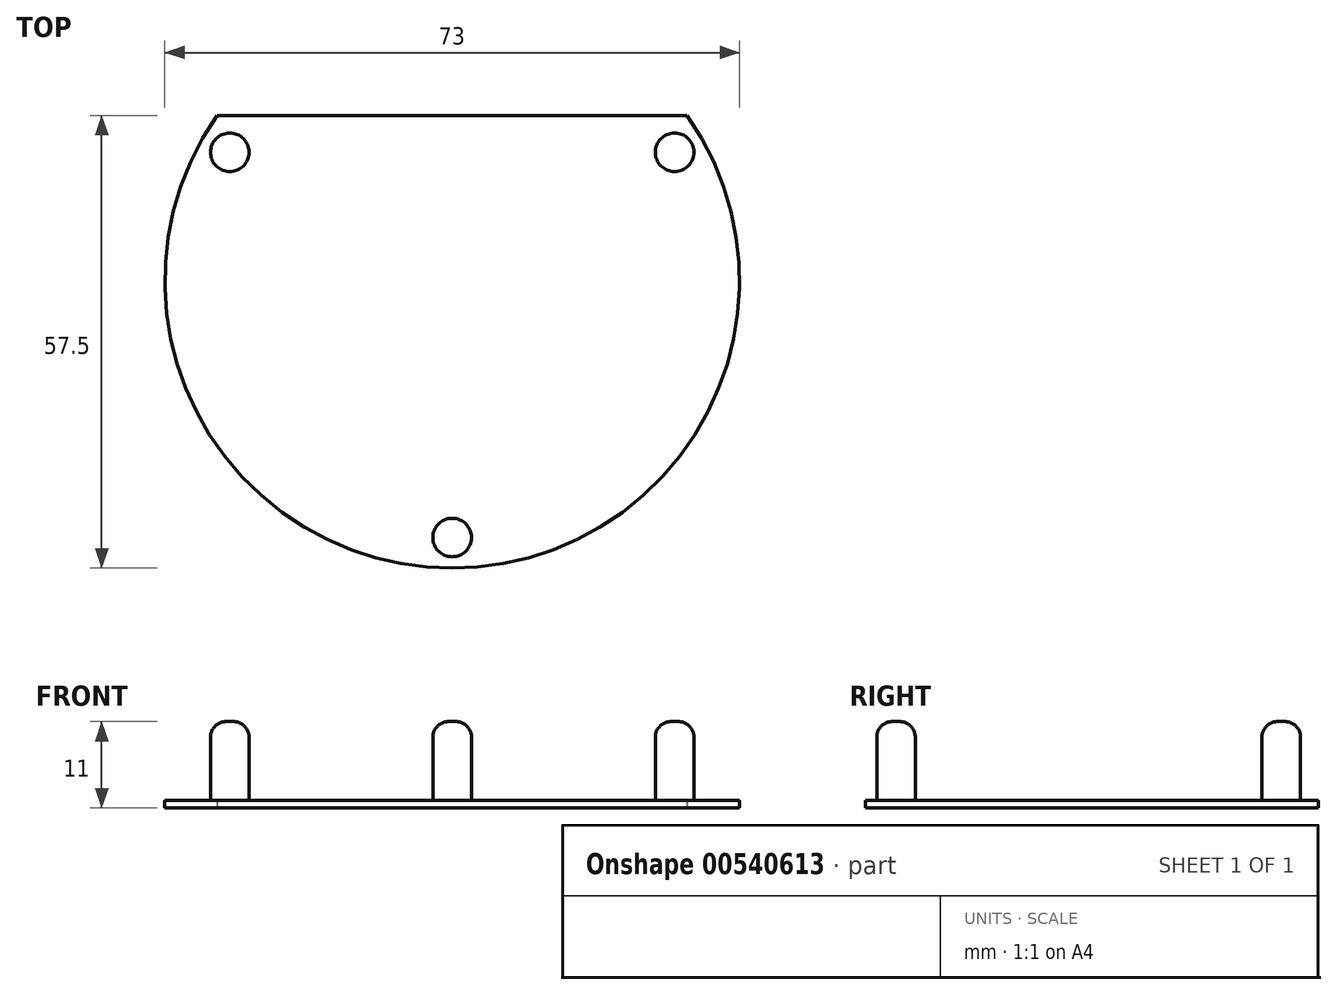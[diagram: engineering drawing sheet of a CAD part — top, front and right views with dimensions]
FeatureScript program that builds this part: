
annotation { "Feature Type Name" : "Feature", "Feature Type Description" : "" }
export const myFeature = defineFeature(function(context is Context, id is Id, definition is map)
    precondition{}
    {
        {
            var Q0;
            Q0=qCreatedBy(makeId("Top.planeOp"),FACE);
            var sketch = newSketch(context, id + "F0", { "sketchPlane" : qUnion([Q0])});
            skArc(sketch, "E0", {"start": v(-29.85, 21) * mm, "mid": v(0, -36.5) * mm, "end": v(29.85, 21) * mm});
            skLineSegment(sketch, "E1", {"start": v(-29.85, 21) * mm, "end": v(29.85, 21) * mm});
            skSolve(sketch);
        }
        {
            var Q0;
            Q0=makeQuery(id+"F0.imprint","IMPRINT",FACE,{"disambiguationData":[TD([[makeQuery(id+"F0.imprint","IMPRINT",EDGE,{"derivedFrom":sQuery(id+"F0.wireOp",EDGE,"E0")}),1.0]])]});
            extrude(context, id + "F1", {"entities" : qUnion([Q0]), "depth" : 1 * mm, "offsetDistance" : 25 * mm});
        }
        {
            var Q0;
            Q0=makeQuery(id+"F1.opExtrude","CAP_FACE",FACE,{"disambiguationData":[OSD([sQuery(id+"F0.wireOp",EDGE,"E0"),sQuery(id+"F0.wireOp",EDGE,"E1")])],"isStart":false});
            var sketch = newSketch(context, id + "F2", { "sketchPlane" : qUnion([Q0])});
            skCircle(sketch, "E2", {"center": v(0, -32.62) * mm, "radius": 2.45 * mm});
            skCircle(sketch, "E3.1.0", {"center": v(-28.25, 16.31) * mm, "radius": 2.45 * mm});
            skCircle(sketch, "E3.2.0", {"center": v(28.25, 16.31) * mm, "radius": 2.45 * mm});
            skPoint(sketch, "E3.center", {"position": v(0, 0) * mm});
            skLineSegment(sketch, "E3.anchor1", {"start": v(0, 0) * mm, "end": v(0, -32.62) * mm, "construction": true});
            skLineSegment(sketch, "E3.anchor2", {"start": v(0, 0) * mm, "end": v(28.25, 16.31) * mm, "construction": true});
            skSolve(sketch);
        }
        {
            var Q0;
            Q0=makeQuery(id+"F2.imprint","IMPRINT",FACE,{"disambiguationData":[TD([[makeQuery(id+"F2.imprint","IMPRINT",EDGE,{"derivedFrom":sQuery(id+"F2.wireOp",EDGE,"E3.1.0")}),1.0]])]});
            var Q1;
            Q1=makeQuery(id+"F2.imprint","IMPRINT",FACE,{"disambiguationData":[TD([[makeQuery(id+"F2.imprint","IMPRINT",EDGE,{"derivedFrom":sQuery(id+"F2.wireOp",EDGE,"E3.2.0")}),1.0]])]});
            var Q2;
            Q2=makeQuery(id+"F2.imprint","IMPRINT",FACE,{"disambiguationData":[TD([[makeQuery(id+"F2.imprint","IMPRINT",EDGE,{"derivedFrom":sQuery(id+"F2.wireOp",EDGE,"E2")}),1.0]])]});
            extrude(context, id + "F3", {"entities" : qUnion([Q0, Q1, Q2]), "operationType" : NewBodyOperationType.ADD, "depth" : 10 * mm, "offsetDistance" : 25 * mm});
        }
        {
            var Q0;
            Q0=makeQuery(id+"F3.opExtrude","CAP_FACE",FACE,{"disambiguationData":[OSD([sQuery(id+"F2.wireOp",EDGE,"E3.1.0")])],"isStart":false});
            var Q1;
            Q1=makeQuery(id+"F3.opExtrude","CAP_EDGE",EDGE,{"disambiguationData":[OSD([sQuery(id+"F2.wireOp",EDGE,"E3.2.0")])],"isStart":false});
            var Q2;
            Q2=makeQuery(id+"F3.opExtrude","CAP_FACE",FACE,{"disambiguationData":[OSD([sQuery(id+"F2.wireOp",EDGE,"E2")])],"isStart":false});
            var Q3;
            Q3=makeQuery(id+"F3.opExtrude","CAP_EDGE",EDGE,{"disambiguationData":[OSD([sQuery(id+"F2.wireOp",EDGE,"E3.1.0")])],"isStart":true});
            var Q4;
            Q4=makeQuery(id+"F3.opExtrude","CAP_EDGE",EDGE,{"disambiguationData":[OSD([sQuery(id+"F2.wireOp",EDGE,"E3.2.0")])],"isStart":true});
            var Q5;
            Q5=makeQuery(id+"F3.opExtrude","CAP_EDGE",EDGE,{"disambiguationData":[OSD([sQuery(id+"F2.wireOp",EDGE,"E2")])],"isStart":true});
            fillet(context, id + "F4", {"entities" : qUnion([Q0, Q1, Q2, Q3, Q4, Q5]), "radius" : 2 * mm, "tangentPropagation" : true, "allowEdgeOverflow" : false});
        }
    });
